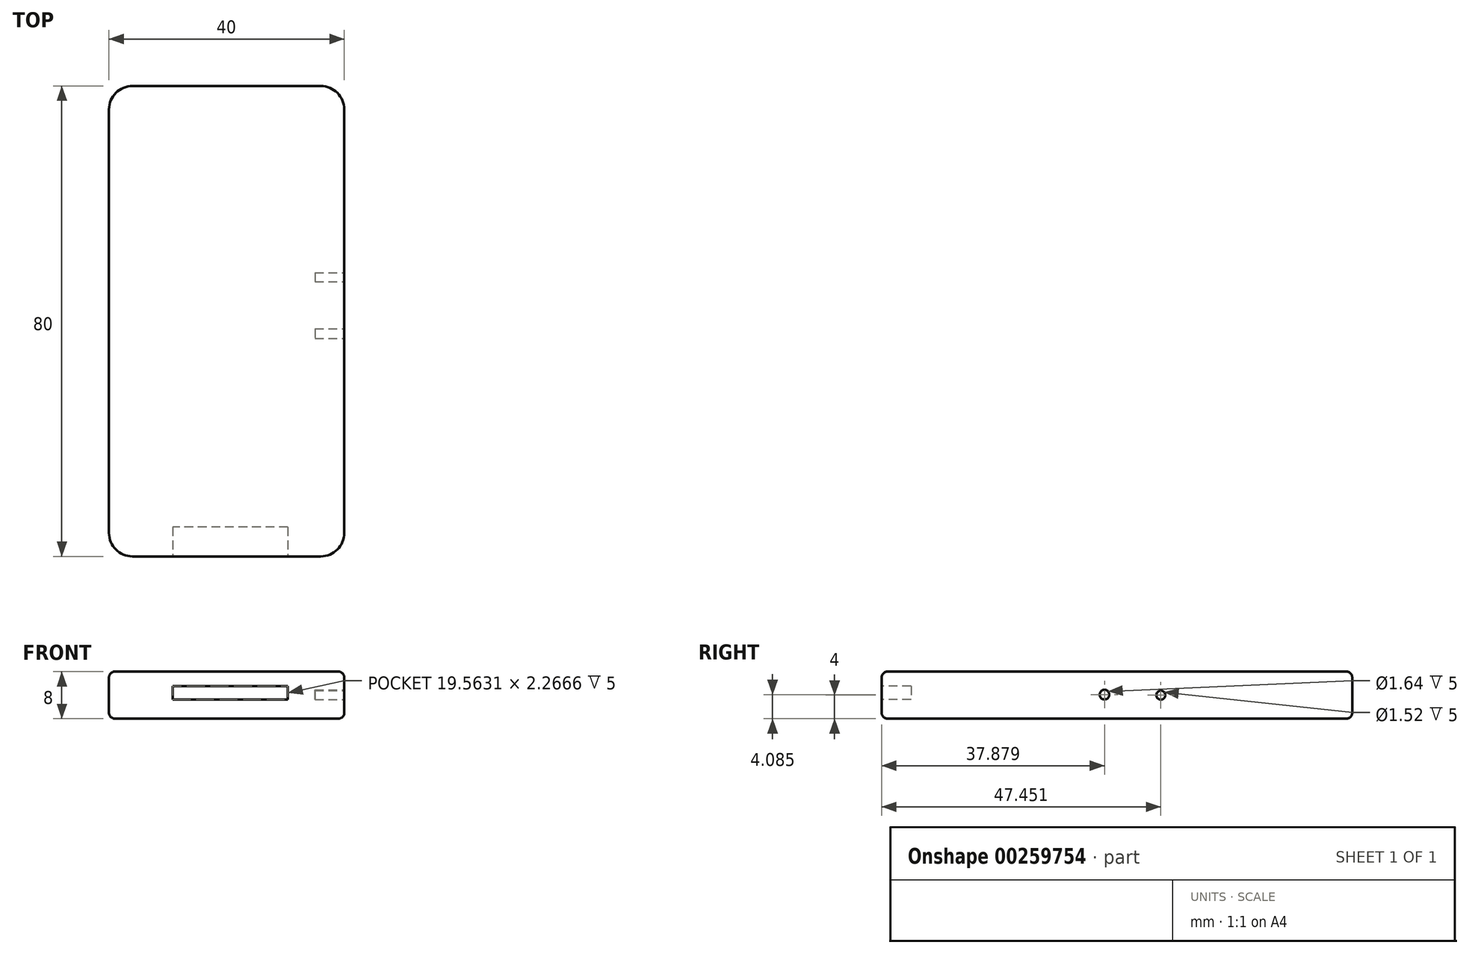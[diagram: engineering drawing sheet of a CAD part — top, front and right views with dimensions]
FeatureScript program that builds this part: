
annotation { "Feature Type Name" : "Feature", "Feature Type Description" : "" }
export const myFeature = defineFeature(function(context is Context, id is Id, definition is map)
    precondition{}
    {
        {
            var Q0;
            Q0=qCreatedBy(makeId("Top.planeOp"),FACE);
            var sketch = newSketch(context, id + "F0", { "sketchPlane" : qUnion([Q0])});
            skLineSegment(sketch, "E0.bottom", {"start": v(-35.96, 43.78) * mm, "end": v(4.04, 43.78) * mm});
            skLineSegment(sketch, "E0.top", {"start": v(-35.96, -36.22) * mm, "end": v(4.04, -36.22) * mm});
            skLineSegment(sketch, "E0.left", {"start": v(-35.96, 43.78) * mm, "end": v(-35.96, -36.22) * mm});
            skLineSegment(sketch, "E0.right", {"start": v(4.04, 43.78) * mm, "end": v(4.04, -36.22) * mm});
            skSolve(sketch);
        }
        {
            var Q0;
            Q0=makeQuery(id+"F0.imprint","IMPRINT",FACE,{"disambiguationData":[TD([[makeQuery(id+"F0.imprint","IMPRINT",EDGE,{"derivedFrom":sQuery(id+"F0.wireOp",EDGE,"E0.bottom")}),-1.0]])]});
            extrude(context, id + "F1", {"entities" : qUnion([Q0]), "depth" : 8 * mm});
        }
        {
            var Q0;
            Q0=makeQuery(id+"F1.opExtrude","SWEPT_EDGE",EDGE,{"disambiguationData":[OSD([sQuery(id+"F0.wireOp",EDGE,"E0.bottom"),sQuery(id+"F0.wireOp",EDGE,"E0.right")])]});
            var Q1;
            Q1=makeQuery(id+"F1.opExtrude","SWEPT_EDGE",EDGE,{"disambiguationData":[OSD([sQuery(id+"F0.wireOp",EDGE,"E0.top"),sQuery(id+"F0.wireOp",EDGE,"E0.right")])]});
            var Q2;
            Q2=makeQuery(id+"F1.opExtrude","SWEPT_EDGE",EDGE,{"disambiguationData":[OSD([sQuery(id+"F0.wireOp",EDGE,"E0.top"),sQuery(id+"F0.wireOp",EDGE,"E0.left")])]});
            var Q3;
            Q3=makeQuery(id+"F1.opExtrude","SWEPT_EDGE",EDGE,{"disambiguationData":[OSD([sQuery(id+"F0.wireOp",EDGE,"E0.bottom"),sQuery(id+"F0.wireOp",EDGE,"E0.left")])]});
            fillet(context, id + "F2", {"entities" : qUnion([Q0, Q1, Q2, Q3]), "radius" : 4 * mm, "tangentPropagation" : true, "allowEdgeOverflow" : false});
        }
        {
            var Q0;
            Q0=makeQuery(id+"F1.opExtrude","CAP_EDGE",EDGE,{"disambiguationData":[OSD([sQuery(id+"F0.wireOp",EDGE,"E0.left")])],"isStart":false});
            var Q1;
            Q1=makeQuery(id+"F1.opExtrude","CAP_EDGE",EDGE,{"disambiguationData":[OSD([sQuery(id+"F0.wireOp",EDGE,"E0.left")])],"isStart":true});
            fillet(context, id + "F3", {"entities" : qUnion([Q0, Q1]), "radius" : 1 * mm, "tangentPropagation" : true, "allowEdgeOverflow" : false});
        }
        {
            var Q0;
            Q0=makeQuery(id+"F1.opExtrude","SWEPT_FACE",FACE,{"disambiguationData":[OSD([sQuery(id+"F0.wireOp",EDGE,"E0.top")])]});
            var sketch = newSketch(context, id + "F4", { "sketchPlane" : qUnion([Q0])});
            skLineSegment(sketch, "E1.bottom", {"start": v(-5.54, 5.53) * mm, "end": v(-25.1, 5.53) * mm});
            skLineSegment(sketch, "E1.top", {"start": v(-5.54, 3.26) * mm, "end": v(-25.1, 3.26) * mm});
            skLineSegment(sketch, "E1.left", {"start": v(-5.54, 5.53) * mm, "end": v(-5.54, 3.26) * mm});
            skLineSegment(sketch, "E1.right", {"start": v(-25.1, 5.53) * mm, "end": v(-25.1, 3.26) * mm});
            skSolve(sketch);
        }
        {
            var Q0;
            Q0=makeQuery(id+"F4.imprint","IMPRINT",FACE,{"disambiguationData":[TD([[makeQuery(id+"F4.imprint","IMPRINT",EDGE,{"derivedFrom":sQuery(id+"F4.wireOp",EDGE,"E1.bottom")}),1.0]])]});
            extrude(context, id + "F5", {"entities" : qUnion([Q0]), "operationType" : NewBodyOperationType.REMOVE, "oppositeDirection" : true, "depth" : 5 * mm});
        }
        {
            var Q0;
            Q0=makeQuery(id+"F1.opExtrude","SWEPT_FACE",FACE,{"disambiguationData":[OSD([sQuery(id+"F0.wireOp",EDGE,"E0.right")])]});
            var sketch = newSketch(context, id + "F6", { "sketchPlane" : qUnion([Q0])});
            skCircle(sketch, "E2", {"center": v(11.23, 4) * mm, "radius": 0.76 * mm});
            skCircle(sketch, "E3", {"center": v(1.66, 4.08) * mm, "radius": 0.82 * mm});
            skSolve(sketch);
        }
        {
            var Q0;
            Q0=makeQuery(id+"F6.imprint","IMPRINT",FACE,{"disambiguationData":[TD([[makeQuery(id+"F6.imprint","IMPRINT",EDGE,{"derivedFrom":sQuery(id+"F6.wireOp",EDGE,"E2")}),1.0]])]});
            var Q1;
            Q1=makeQuery(id+"F6.imprint","IMPRINT",FACE,{"disambiguationData":[TD([[makeQuery(id+"F6.imprint","IMPRINT",EDGE,{"derivedFrom":sQuery(id+"F6.wireOp",EDGE,"E3")}),1.0]])]});
            extrude(context, id + "F7", {"entities" : qUnion([Q0, Q1]), "operationType" : NewBodyOperationType.REMOVE, "oppositeDirection" : true, "depth" : 5 * mm});
        }
    });
